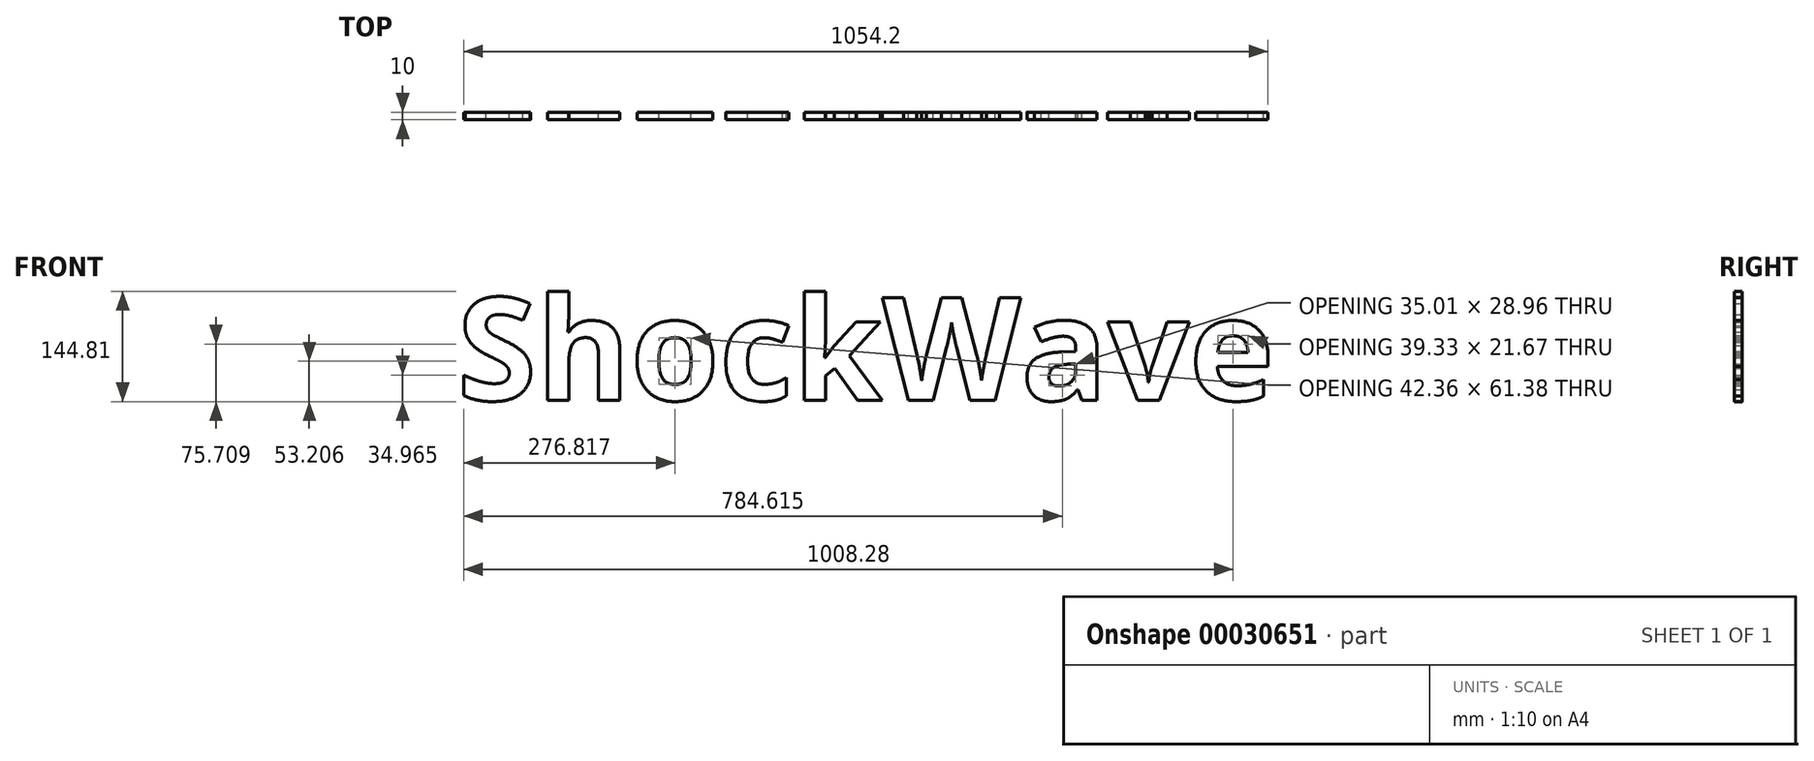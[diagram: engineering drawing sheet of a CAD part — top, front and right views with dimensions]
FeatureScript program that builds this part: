
annotation { "Feature Type Name" : "Feature", "Feature Type Description" : "" }
export const myFeature = defineFeature(function(context is Context, id is Id, definition is map)
    precondition{}
    {
        {
            var Q0;
            Q0=qCreatedBy(makeId("Front.planeOp"),FACE);
            var sketch = newSketch(context, id + "F0", { "sketchPlane" : qUnion([Q0])});
            skText(sketch, "E0", { "text": "ShockWave", "fontName": "OpenSans-Bold.ttf"});
            const initialGuessF0  = {"E0": [-0.50187, -0.05854, 1, 0, 0.13546]};
            skSetInitialGuess(sketch, initialGuessF0);
            skSolve(sketch);
        }
        {
            var Q0;
            Q0 = qSketchRegion(id + "F0", true);
            extrude(context, id + "F1", {"entities" : qUnion([Q0]), "depth" : 10 * mm});
        }
    });
